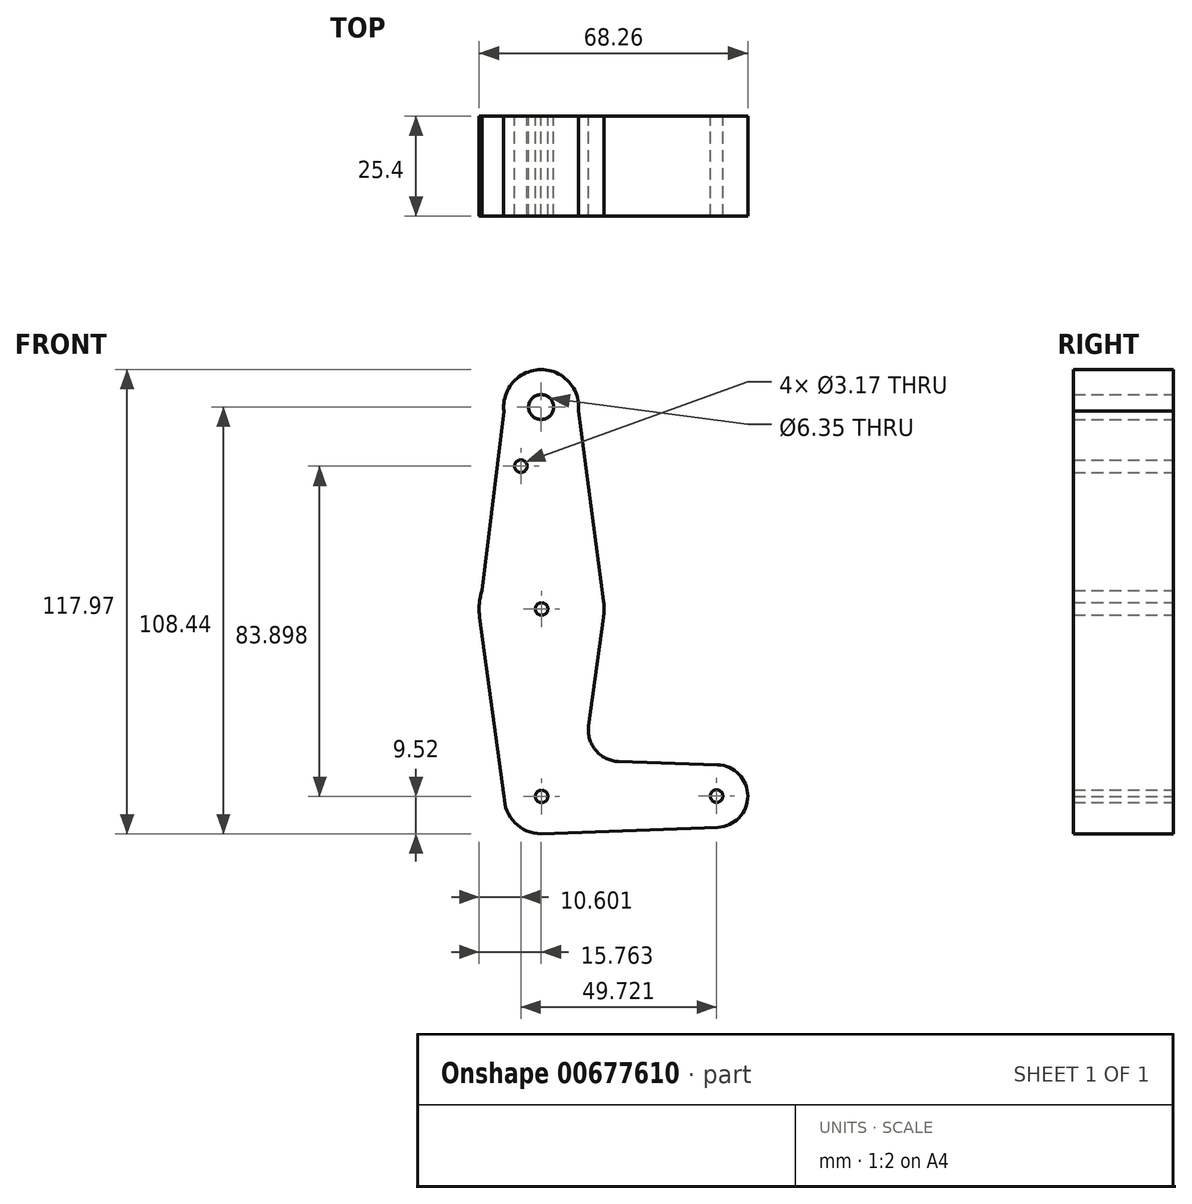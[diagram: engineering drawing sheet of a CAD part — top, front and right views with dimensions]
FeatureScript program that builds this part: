
annotation { "Feature Type Name" : "Feature", "Feature Type Description" : "" }
export const myFeature = defineFeature(function(context is Context, id is Id, definition is map)
    precondition{}
    {
        {
            var Q0;
            Q0=qCreatedBy(makeId("Front.planeOp"),FACE);
            var sketch = newSketch(context, id + "F0", { "sketchPlane" : qUnion([Q0])});
            skCircle(sketch, "E0", {"center": v(9.47, 82.54) * mm, "radius": 9.53 * mm});
            skCircle(sketch, "E1", {"center": v(9.58, -16.38) * mm, "radius": 9.53 * mm});
            skCircle(sketch, "E2", {"center": v(54.03, -16.3) * mm, "radius": 7.94 * mm});
            skLineSegment(sketch, "E3", {"start": v(9.47, -25.9) * mm, "end": v(54.33, -24.24) * mm});
            skLineSegment(sketch, "E4", {"start": v(29.15, -7.52) * mm, "end": v(54.33, -8.37) * mm});
            skCircle(sketch, "E5", {"center": v(9.47, 82.54) * mm, "radius": 3.18 * mm});
            skCircle(sketch, "E6", {"center": v(9.58, 31.25) * mm, "radius": 15.88 * mm});
            skLineSegment(sketch, "E7", {"start": v(0.06, -16.38) * mm, "end": v(-6.15, 29.1) * mm});
            skLineSegment(sketch, "E8", {"start": v(25.31, 29.1) * mm, "end": v(21.55, 1.5) * mm});
            skLineSegment(sketch, "E9", {"start": v(-6.15, 31.25) * mm, "end": v(0, 81.55) * mm});
            skLineSegment(sketch, "E10", {"start": v(18.95, 81.58) * mm, "end": v(25.32, 33.32) * mm});
            skCircle(sketch, "E11", {"center": v(4.31, 67.52) * mm, "radius": 1.59 * mm});
            skCircle(sketch, "E12", {"center": v(9.58, 31.25) * mm, "radius": 1.59 * mm});
            skCircle(sketch, "E13", {"center": v(9.58, -16.38) * mm, "radius": 1.59 * mm});
            skCircle(sketch, "E14", {"center": v(54.03, -16.3) * mm, "radius": 1.59 * mm});
            skArc(sketch, "E15.filletArc", {"start": v(21.55, 1.5) * mm, "mid": v(23.35, -4.7) * mm, "end": v(29.15, -7.52) * mm});
            skSolve(sketch);
        }
        {
            var Q0;
            {var subQ0=sQuery(id+"F0.wireOp",EDGE,"E10");Q0=makeQuery(id+"F0.imprint","IMPRINT",FACE,{"disambiguationData":[TD([[makeQuery(id+"F0.imprint","IMPRINT",EDGE,{"derivedFrom":subQ0}),-1.0]])]});}
            var Q1;
            Q1=makeQuery(id+"F0.imprint","IMPRINT",FACE,{"disambiguationData":[TD([[makeQuery(id+"F0.imprint","IMPRINT",EDGE,{"derivedFrom":sQuery(id+"F0.wireOp",EDGE,"E5")}),-1.0]])]});
            var Q2;
            Q2=makeQuery(id+"F0.imprint","IMPRINT",FACE,{"disambiguationData":[TD([[makeQuery(id+"F0.imprint","IMPRINT",EDGE,{"derivedFrom":sQuery(id+"F0.wireOp",EDGE,"E13")}),-1.0]])]});
            var Q3;
            Q3=makeQuery(id+"F0.imprint","IMPRINT",FACE,{"disambiguationData":[TD([[makeQuery(id+"F0.imprint","IMPRINT",EDGE,{"derivedFrom":sQuery(id+"F0.wireOp",EDGE,"E12")}),-1.0]])]});
            var Q4;
            {var subQ5=sQuery(id+"F0.wireOp",EDGE,"E4");Q4=makeQuery(id+"F0.imprint","IMPRINT",FACE,{"disambiguationData":[TD([[makeQuery(id+"F0.imprint","IMPRINT",EDGE,{"derivedFrom":subQ5}),-1.0]])]});}
            var Q5;
            Q5=makeQuery(id+"F0.imprint","IMPRINT",FACE,{"disambiguationData":[TD([[makeQuery(id+"F0.imprint","IMPRINT",EDGE,{"derivedFrom":sQuery(id+"F0.wireOp",EDGE,"E14")}),-1.0]])]});
            extrude(context, id + "F1", {"entities" : qUnion([Q0, Q1, Q2, Q3, Q4, Q5]), "depth" : 25.4 * mm, "offsetDistance" : 25.4 * mm});
        }
    });
